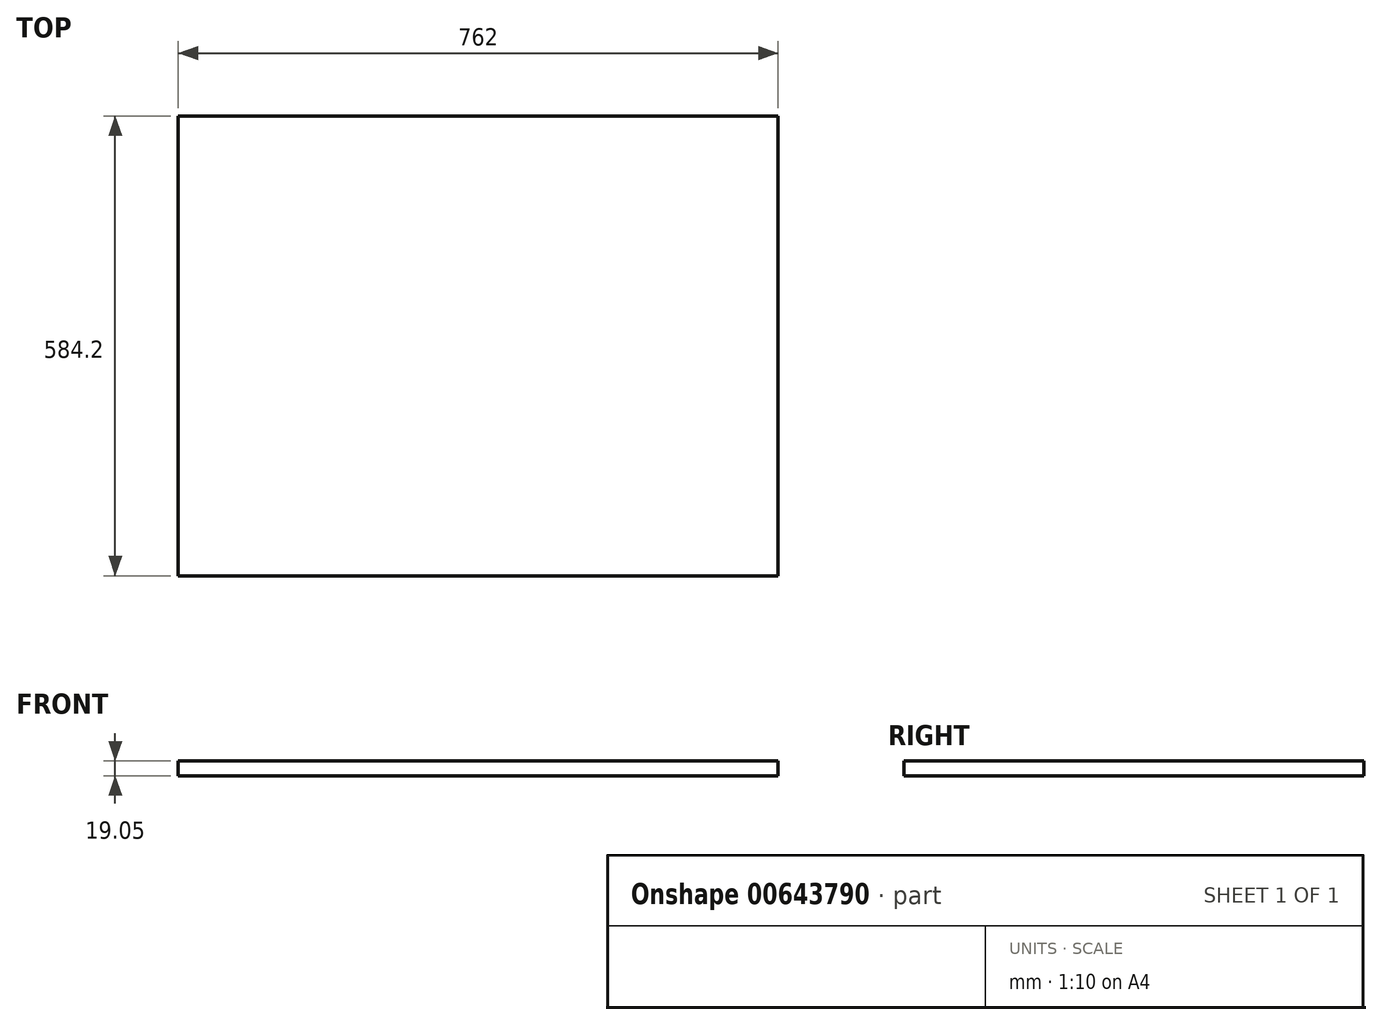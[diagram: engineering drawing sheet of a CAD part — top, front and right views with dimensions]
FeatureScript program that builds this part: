
annotation { "Feature Type Name" : "Feature", "Feature Type Description" : "" }
export const myFeature = defineFeature(function(context is Context, id is Id, definition is map)
    precondition{}
    {
        {
            var Q0;
            Q0=qCreatedBy(makeId("Top.planeOp"),FACE);
            var sketch = newSketch(context, id + "F0", { "sketchPlane" : qUnion([Q0])});
            skLineSegment(sketch, "E0.bottom", {"start": v(381, 292.1) * mm, "end": v(-381, 292.1) * mm});
            skLineSegment(sketch, "E0.top", {"start": v(381, -292.1) * mm, "end": v(-381, -292.1) * mm});
            skLineSegment(sketch, "E0.left", {"start": v(381, 292.1) * mm, "end": v(381, -292.1) * mm});
            skLineSegment(sketch, "E0.right", {"start": v(-381, 292.1) * mm, "end": v(-381, -292.1) * mm});
            skPoint(sketch, "E0.middle", {"position": v(0, 0) * mm});
            skSolve(sketch);
        }
        {
            var Q0;
            Q0=makeQuery(id+"F0.imprint","IMPRINT",FACE,{"disambiguationData":[TD([[makeQuery(id+"F0.imprint","IMPRINT",EDGE,{"derivedFrom":sQuery(id+"F0.wireOp",EDGE,"E0.bottom")}),1.0]])]});
            extrude(context, id + "F1", {"entities" : qUnion([Q0]), "depth" : 19.05 * mm, "offsetDistance" : 25.4 * mm});
        }
    });
